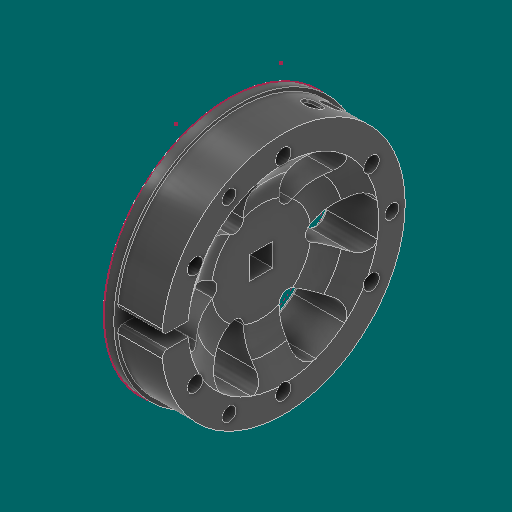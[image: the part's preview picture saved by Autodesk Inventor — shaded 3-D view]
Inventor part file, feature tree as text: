
AUTODESK INVENTOR PART (.ipt)
format: ipt  version: 2023.1 (Build 271208000, 208)  size: 572,416 bytes
history: native  units: in
note: dims shown in document units (in); Inventor stores cm internally (conversion verified against a paired STEP export)
features: sketch x5, other x3
ambient origin geometry x8: Origin, YZ Plane, XZ Plane, XY Plane, X Axis, Y Axis, Z Axis, Center Point
bodies: Solid1 (feature_tree)
feature tree (8):
  other  "WheelHalf_MIR.ipt"
  other  "Solid1::WheelHalf_MIR.ipt"
  other  "TaggingFeature1"
  sketch  "Sketch1"  dims[d0=0.3937in]
  sketch  "Sketch2"
  sketch  "Sketch3"
  sketch  "Sketch4"
  sketch  "Sketch5"
